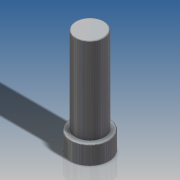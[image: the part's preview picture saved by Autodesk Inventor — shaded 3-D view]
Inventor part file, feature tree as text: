
AUTODESK INVENTOR PART (.ipt)
format: ipt  version: 2016 SP2 (Build 200236200, 236)  size: 122,880 bytes
history: native  units: in
note: dims shown in document units (in); Inventor stores cm internally (conversion verified against a paired STEP export)
features: revolve x1, fillet x1, sketch x1
ambient origin geometry x8: Origin, YZ Plane, XZ Plane, XY Plane, X Axis, Y Axis, Z Axis, Center Point
bodies: Solid1 (feature_tree)
feature tree (3):
  revolve  "Revolution1"  [1 undecoded]
  fillet  "Fillet1"  Radius=0.063in
  sketch  "Sketch2"  dims[d0=0.126in d1=0.0945in d2=0.063in d3=0.2835in d4=90.0deg d5=0.0039in]
note: 1 required parameter value undecoded (feature->parameter linkage not recoverable at this tier; creation-order binding heuristic only, values carry confidence <= 0.55)
